# Revit family: IS_Conca_T4107_BIM_IT
name_source: partatom
category: Plumbing Fixtures
revit_build: Autodesk Revit 2017 (Build: 20160225_1515(x64)
units: mm (PartAtom-declared; Revit-internal decimal feet)

## family parameters
Always vertical = No
Cut with Voids When Loaded = No
OmniClass Number = 23.45.05.14.21.11
OmniClass Title = Bath/Shower Units
Part Type = Normal
Room Calculation Point = No
Round Connector Dimension = Use Diameter
Shared = No
Work Plane-Based = No

## types (6) — shared parameters
Accessori = https://www.idealstandard.it
Aiuto = https://www.idealstandard.it
AltezzaNominale = 1401 mm
Autore = Ideal Standard
BIMobject category = Storage
BIMobject category code = sanitary-storage
BIMobject main category = Sanitary
BIMobject main category code = sanitary
Brand = https://www.idealstandard.it
Caratteristiche = Doppia semi colonna 720x250x1400mm dotata di due porte con sistema di chiusura rallentata e apertura push to open. Dotata di 4 ripiani fissii.
Description = Double semi-column 720x250x1400mm equipped with two doors with slow closing system and push to open opening. Equipped with 4 fixed shelves.
DescrizioneClassifcazioneUni2015 = Bathroom cabinets
Desrizione = Doppia semi colonna 720x250x1400mm dotata di due porte con sistema di chiusura rallentata e apertura push to open. Dotata di 4 ripiani fissii.
DurataGaranzia = 2
DurataGaranziaProdotti = 2
Forma = Rettangolare
Garanzia = Garanzia Idealstandard
IfcEsportaCome = IfcFurnitureType
InformaziniGaranzia = https://www.idealstandard.it
InformazioniDiProdotto = http://www.idealstandard.it
InformazioniGaranzia = https://www.idealstandard.it
Installation instructions = https://www.idealspec.co.uk
InstruzioniInstallazione = https://www.idealstandard.it
LarghezzaNominale = 716 mm  [stored 2.34908 ft]
Maniglia = No
Manufacturer = Ideal Standard
Materiale = Ceramics
NominalDepth = 250 mm  [stored 0.82021 ft]
NominalHeight = 1401 mm
NominalWidth = 716 mm  [stored 2.34908 ft]
PesoNetto = 46.5
PiattoDoccia = No
Product group = Bathroom_Furniture
Produttore = Ideal Standard
ProfonditaNominale = 250 mm  [stored 0.82021 ft]
Revisione = 1
RiferimentoClassificazioneUni2015 = Pr_40_30_78_03
Spazio = Interno
Telefono = 800 652 290
TipoEspotazioneIfc = Bathroom cabinets
URL = https://www.ideal-standard.co.uk
Uniclass 2015 Code = Pr_40_30_78_03
Uniclass 2015 Name = Bathroom cabinets
UnitàDurata = Anno
UnitàDurataGaranzia = Anno
UnitàLineare = Milimitre
UnitàMonetaria = €
UnitàSuperficie = Milimitre
UnitàVolume = Litri
Versione = 1
VersioneClassificazioneUni2015 = v1.1
zero-valued in all types: CostoDiSostituzione, DimensioneScarico, LunghezzaNominale, Nominal depth, Nominal height, SeatMaterial, SpessoreDelMateriale, SpilloverLivello, Weight Net (Kg)

## per-type parameters (varying)
| type | CodiceABarre | CodiceArticolo | Colore | Finitura | Model | ModelloDiRiferimento | Nome | NomeOggettoBim | NumeroDiModello |
| T4107Y1 - DOUBLE 1/2 COLM  WHMT | 8014140463214 | T4107Y1 | Matt white | Matt white | T4107Y1 | T4107Y1 | BathroomCabinets_Conca_T4107Y1_IdealStandard | ISI_IdealStandard_Bathroom Cabinets_Conca_T4107Y1 | T4107Y1 |
| T4107Y2 - DOUBLE 1/2 COLM  ANMT | 8014140463221 | T4107Y2 | Matt anthracite | Matt anthracite | T4107Y2 | T4107Y2 | BathroomCabinets_Conca_T4107Y2_IdealStandard | ISI_IdealStandard_Bathroom Cabinets_Conca_T4107Y2 | T4107Y2 |
| T4107Y3 - DOUBLE 1/2 COLM  SNMT | 8014140463238 | T4107Y3 | Matt Sunset | Matt Sunset | T4107Y3 | T4107Y3 | BathroomCabinets_Conca_T4107Y3_IdealStandard | ISI_IdealStandard_Bathroom Cabinets_Conca_T4107Y3 | T4107Y3 |
| T4107Y4 - DOUBLE 1/2 COLM   SMOK | 8014140463245 | T4107Y4 | Matt Sunset | Matt Sunset | T4107Y4 | T4107Y4 | BathroomCabinets_Conca_T4107Y4_IdealStandard | ISI_IdealStandard_Bathroom Cabinets_Conca_T4107Y4 | T4107Y4 |
| T4107Y5 - DOUBLE 1/2 COLM   DKWN | 8014140463252 | T4107Y5 | Dark Walnut | Dark Walnut | T4107Y5 | T4107Y5 | BathroomCabinets_Conca_T4107Y5_IdealStandard | ISI_IdealStandard_Bathroom Cabinets_Conca_T4107Y5 | T4107Y5 |
| T4107Y6 - DOUBLE 1/2 COLM  LTOK | 8014140463269 | T4107Y6 | Light Oak | Light Oak | T4107Y6 | T4107Y6 | BathroomCabinets_Conca_T4107Y6_IdealStandard | ISI_IdealStandard_Bathroom Cabinets_Conca_T4107Y6 | T4107Y6 |

note: [stored X ft] marks values corroborated as IEEE doubles in the binary element streams (Revit-internal decimal feet)

## geometry (parser evidence)
native form markers: Sweep x3
no freeform markers — native parametric forms only
